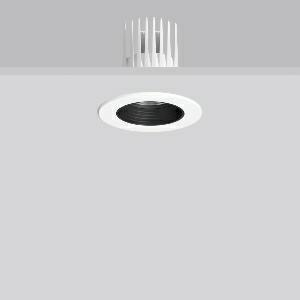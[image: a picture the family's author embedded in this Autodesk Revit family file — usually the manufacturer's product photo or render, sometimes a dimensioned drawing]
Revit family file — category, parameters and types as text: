
# Revit family: heledon_mini_e_901743_002_1_3dbf
name_source: partatom
category: Lighting Fixtures
units: mm (PartAtom-declared; Revit-internal decimal feet)

## family parameters
Cut with Voids When Loaded = No
Host = Face
Light Source = No
Part Type = Normal
Room Calculation Point = No
Round Connector Dimension = Use Diameter
Shared = No

## types (1)
- HELEDON mini E (1 x LED Modul 940, 2400 lm, 4000)
    Apparent Load = 20 VA
    Approval mark = CE
    CIE Flux Codes = 99 100 100 100 100
    Color Rendering = 92
    Color Temperature = 4000
    Default Elevation = 1800 mm
    Description = Series: HELEDON mini
Round recessed downlight. Housing: die-cast aluminium, powder-coated. Black plastic ring and recessed LED to prevent glare from the side. Optical assembly with lens made of plastic (polycarbonate) for the best homogeneous light distribution - can be changed without tools. Best colour rendering index Ra>90. Suitable for Recessed ceiling mounting. Installation without tools thanks to spring fastening system. Including separate LED converter with connecting cable 600 mm.High quality converter without flickering and stroboscopic effect. Through-wiring box (5 pole) available as accessory. The following accessories can be mounted without use of tools: interchangeable lenses, decorative glasses, honeycomb louvre, clear and frosted diffusers, white interchangeable plastic ring. 
Colour: traffic white, matt (RAL 9016)
Diameter: 124 mm
Height: 3 mm
Cut-out diameter: 114 mm
Recess height: 170 mm
Luminaire: recess height: 120 mm
Lamp: LED
Socket: without socket
Colour temperature: 4000K
Colour rendering index (CRI): 92
System power: 20 W
Rated luminous flux: 2400 lm
Luminous efficiency: 120 lm/W
Control gear: Regulated power supply
Protection class: II
Type of protection: IP 20
    Height = 0 mm  [stored 0 ft]
    Lamp = 1 x LED Modul 940
    Lamp Light Flux = 2400 lm
    Lamp count = 1
    Length = 124 mm  [stored 0.406824 ft]
    Lifetime = 50000 h
    Luminous efficacy = 120 lm/W
    Manufacturer = RZB
    ModVariant = No
    Model = 901743.002.1
    Mounting Place = Ceiling
    Mounting Type = Recessed
    Number of Poles = 1
    OnlyDefault = Yes
    Power Factor = 1
    Product Name = HELEDON mini E
    Product group = Recessed downlights
    ProductGroupID = 402
    Protection Class = Protection class II
    Protection Degree = IP 20
    RLX_Detail_Level = 1
    RLX_Emergency_Light_Flux = 0 lm
    RLX_Emergency_Type = 0
    RLX_Emergency_Type_DB = No
    RlxData = <blob elided: 129165 chars, md5=a397a69a>
    Socket = socket
    Standby Power = 0 W
    System Light Flux = 2400 lm
    System Power = 20 W
    Type Comments = Product without accessories
    Type Image = 901656.002.jpg
    URL = http://relux.com
    VarID = ---
    Voltage = 230 V
    Voltage Range = 220-240 V
    Weight = 0.00 kg
    Width = 0 mm  [stored 0 ft]

note: [stored X ft] marks values corroborated as IEEE doubles in the binary element streams (Revit-internal decimal feet)

## geometry (parser evidence)
native form markers: Blend x4, Sweep x12
no freeform markers — native parametric forms only
